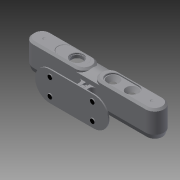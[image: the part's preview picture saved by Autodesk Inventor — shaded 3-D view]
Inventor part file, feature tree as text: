
AUTODESK INVENTOR PART (.ipt)
format: ipt  version: 2013 (Build 170138000, 138)  size: 464,896 bytes
history: native  units: mm
features: extrude x13, chamfer x13, sketch x13, fillet x9, other x3
ambient origin geometry x8: Origin, YZ Plane, XZ Plane, XY Plane, X Axis, Y Axis, Z Axis, Center Point
feature tree (51):
  other  "ソリッド1"
  extrude  "押し出し1"  Depth=25.0mm
  chamfer  "面取り1"  Distance=12.5mm
  extrude  "押し出し6"  Depth=25.0mm
  chamfer  "面取り7"  Distance=154.0mm
  chamfer  "面取り9"  Distance=79.0mm
  fillet  "フィレット4"  Radius=34.5mm
  chamfer  "面取り11"  Distance=2.0mm Angle=45.0deg
  fillet  "フィレット5"  Radius=57.5mm
  fillet  "フィレット6"  Radius=61.5mm
  chamfer  "面取り12"  Distance=12.5mm
  extrude  "押し出し7"  Depth=12.5mm
  extrude  "押し出し8"  Depth=1.5mm TaperAngle=0.0deg
  chamfer  "面取り13"  Distance=1.5mm Angle=45.0deg
  fillet  "フィレット7"  Radius=1.5mm
  chamfer  "面取り14"  Distance=15.0mm
  extrude  "押し出し9"  Depth=2.5mm TaperAngle=30.0deg
  chamfer  "面取り15"  Distance=40.0mm
  chamfer  "面取り16"  Distance=12.0mm
  extrude  "押し出し10"  Depth=2.5mm TaperAngle=30.0deg
  extrude  "押し出し11"  Depth=19.0mm
  chamfer  "面取り17"  Distance=10.0mm
  fillet  "フィレット8"  Radius=10.0mm
  extrude  "押し出し12"  Depth=22.0mm
  fillet  "フィレット9"  Radius=22.0mm
  extrude  "押し出し13"  Depth=10.0mm
  chamfer  "面取り18"  Distance=10.0mm
  extrude  "押し出し14"  Depth=3.5mm
  chamfer  "面取り19"  Distance=3.5mm
  extrude  "押し出し15"  Depth=4.0mm
  fillet  "フィレット10"  Radius=0.5mm
  extrude  "押し出し16"  Depth=18.0mm
  fillet  "フィレット11"  Radius=10.0mm
  chamfer  "面取り21"  Distance=10.0mm
  extrude  "押し出し17"  Depth=26.0mm
  fillet  "フィレット12"  Radius=22.0mm
  sketch  "スケッチ1"
  sketch  "スケッチ7"
  sketch  "スケッチ8"
  sketch  "スケッチ10"
  sketch  "スケッチ11"
  sketch  "スケッチ12"
  sketch  "スケッチ13"
  sketch  "スケッチ14"
  sketch  "スケッチ15"
  sketch  "スケッチ16"
  sketch  "スケッチ17"
  sketch  "スケッチ18"
  sketch  "スケッチ19"
  other  "断面エッジを投影1"
  other  "断面エッジを投影2"
